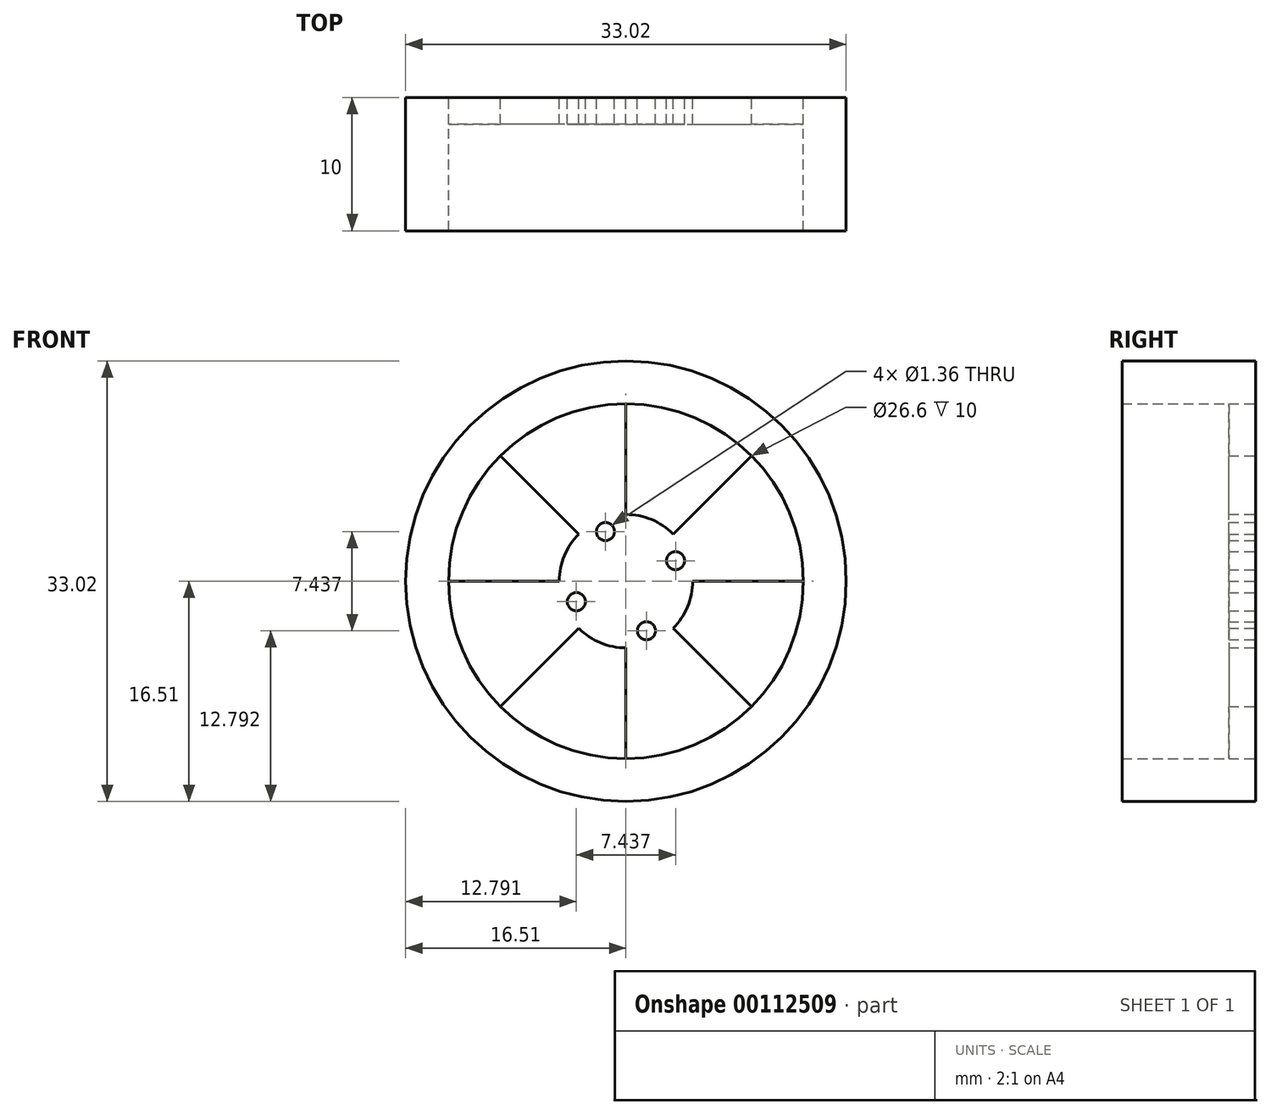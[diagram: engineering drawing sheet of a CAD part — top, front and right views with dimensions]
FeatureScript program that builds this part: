
annotation { "Feature Type Name" : "Feature", "Feature Type Description" : "" }
export const myFeature = defineFeature(function(context is Context, id is Id, definition is map)
    precondition{}
    {
        {
            var Q0;
            Q0=qCreatedBy(makeId("Front.planeOp"),FACE);
            var sketch = newSketch(context, id + "F0", { "sketchPlane" : qUnion([Q0])});
            skCircle(sketch, "E0", {"center": v(0, 0) * mm, "radius": 16.51 * mm});
            skCircle(sketch, "E1", {"center": v(0, 0) * mm, "radius": 5 * mm});
            skCircle(sketch, "E2", {"center": v(0, 0) * mm, "radius": 13.3 * mm});
            skLineSegment(sketch, "E3", {"start": v(-5, 0) * mm, "end": v(-13.3, 0) * mm});
            skLineSegment(sketch, "E4", {"start": v(-3.54, -3.54) * mm, "end": v(-9.4, -9.4) * mm});
            skLineSegment(sketch, "E5", {"start": v(0, -5) * mm, "end": v(0, -13.3) * mm});
            skLineSegment(sketch, "E6", {"start": v(3.54, -3.54) * mm, "end": v(9.4, -9.4) * mm});
            skLineSegment(sketch, "E7", {"start": v(5, 0) * mm, "end": v(13.3, 0) * mm});
            skLineSegment(sketch, "E8", {"start": v(3.54, 3.54) * mm, "end": v(9.4, 9.4) * mm});
            skLineSegment(sketch, "E9", {"start": v(0, 5) * mm, "end": v(0, 13.3) * mm});
            skLineSegment(sketch, "E10", {"start": v(-3.54, 3.54) * mm, "end": v(-9.4, 9.4) * mm});
            skCircle(sketch, "E11", {"center": v(-1.54, 3.72) * mm, "radius": 0.68 * mm});
            skCircle(sketch, "E12", {"center": v(-3.72, -1.54) * mm, "radius": 0.68 * mm});
            skCircle(sketch, "E13", {"center": v(1.54, -3.72) * mm, "radius": 0.68 * mm});
            skCircle(sketch, "E14", {"center": v(3.72, 1.54) * mm, "radius": 0.68 * mm});
            skCircle(sketch, "E15", {"center": v(-1.54, 3.72) * mm, "radius": 0.54 * mm});
            skCircle(sketch, "E16", {"center": v(3.72, 1.54) * mm, "radius": 0.54 * mm});
            skCircle(sketch, "E17", {"center": v(1.54, -3.72) * mm, "radius": 0.54 * mm});
            skCircle(sketch, "E18", {"center": v(-3.72, -1.54) * mm, "radius": 0.54 * mm});
            skSolve(sketch);
        }
        {
            var Q0;
            Q0=makeQuery(id+"F0.imprint","IMPRINT",FACE,{"disambiguationData":[TD([[makeQuery(id+"F0.imprint","IMPRINT",EDGE,{"derivedFrom":sQuery(id+"F0.wireOp",EDGE,"E0")}),1.0]])]});
            extrude(context, id + "F1", {"entities" : qUnion([Q0]), "depth" : 10 * mm});
        }
        {
            var Q0;
            {var subQ0=sQuery(id+"F0.wireOp",EDGE,"E9");Q0=makeQuery(id+"F0.imprint","IMPRINT",FACE,{"disambiguationData":[TD([[makeQuery(id+"F0.imprint","IMPRINT",EDGE,{"derivedFrom":subQ0}),1.0]])]});}
            var Q1;
            Q1=makeQuery(id+"F0.imprint","IMPRINT",FACE,{"disambiguationData":[TD([[makeQuery(id+"F0.imprint","IMPRINT",EDGE,{"derivedFrom":sQuery(id+"F0.wireOp",EDGE,"E11")}),-1.0]])]});
            var Q2;
            {var subQ1=sQuery(id+"F0.wireOp",EDGE,"E7");Q2=makeQuery(id+"F0.imprint","IMPRINT",FACE,{"disambiguationData":[TD([[makeQuery(id+"F0.imprint","IMPRINT",EDGE,{"derivedFrom":subQ1}),1.0]])]});}
            var Q3;
            {var subQ0=sQuery(id+"F0.wireOp",EDGE,"E5");Q3=makeQuery(id+"F0.imprint","IMPRINT",FACE,{"disambiguationData":[TD([[makeQuery(id+"F0.imprint","IMPRINT",EDGE,{"derivedFrom":subQ0}),1.0]])]});}
            var Q4;
            {var subQ0=sQuery(id+"F0.wireOp",EDGE,"E4");Q4=makeQuery(id+"F0.imprint","IMPRINT",FACE,{"disambiguationData":[TD([[makeQuery(id+"F0.imprint","IMPRINT",EDGE,{"derivedFrom":subQ0}),-1.0]])]});}
            extrude(context, id + "F2", {"entities" : qUnion([Q0, Q1, Q2, Q3, Q4]), "operationType" : NewBodyOperationType.ADD, "depth" : 2 * mm});
        }
    });
